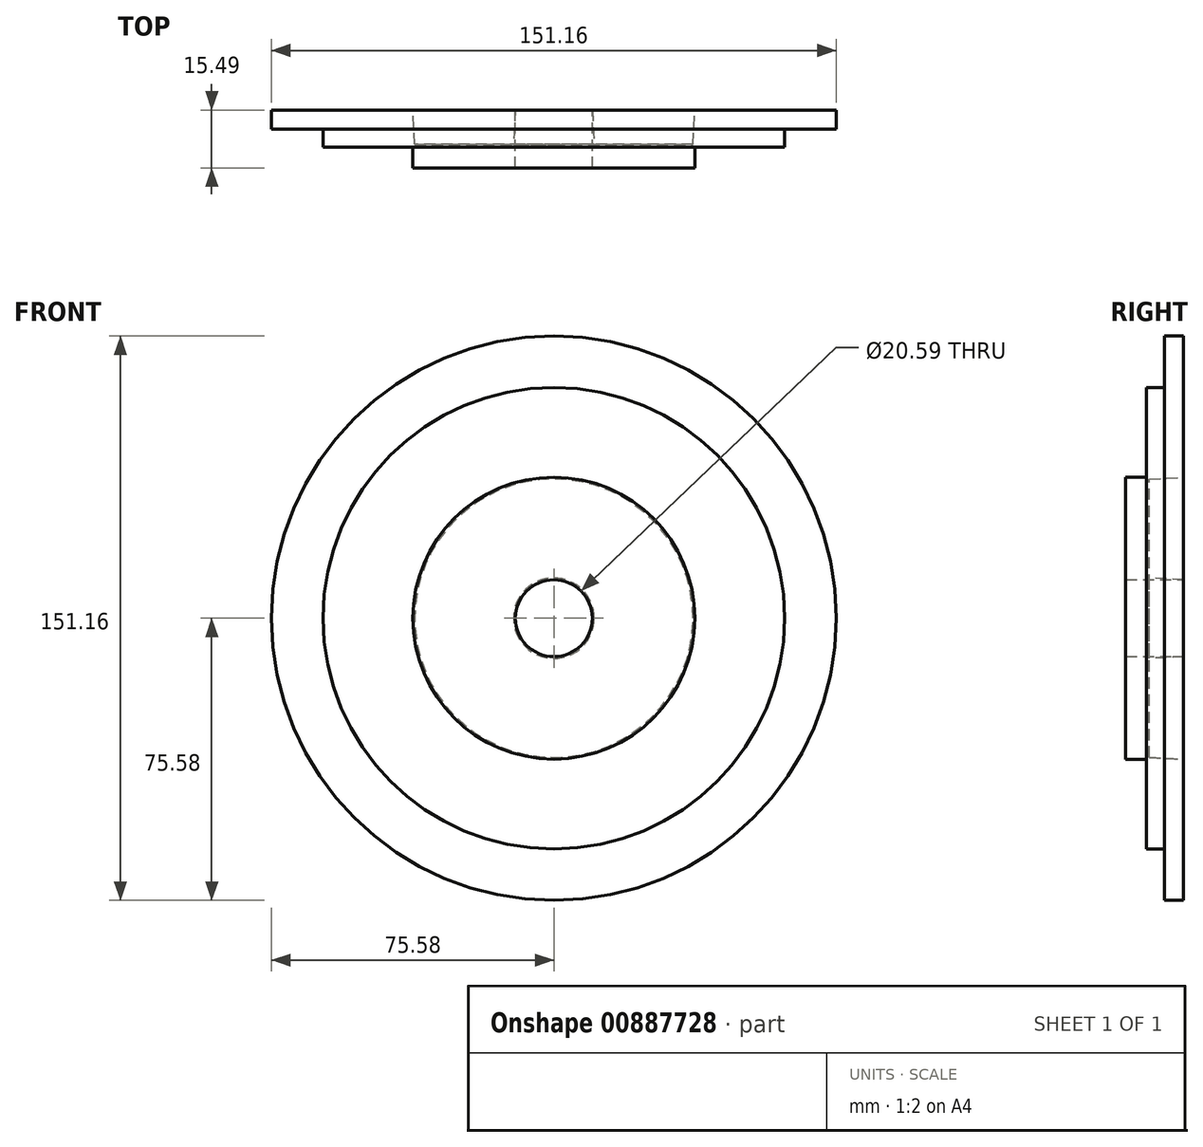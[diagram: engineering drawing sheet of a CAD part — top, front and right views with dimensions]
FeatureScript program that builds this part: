
annotation { "Feature Type Name" : "Feature", "Feature Type Description" : "" }
export const myFeature = defineFeature(function(context is Context, id is Id, definition is map)
    precondition{}
    {
        {
            var Q0;
            Q0=qCreatedBy(makeId("Front.planeOp"),FACE);
            var sketch = newSketch(context, id + "F0", { "sketchPlane" : qUnion([Q0])});
            skCircle(sketch, "E0", {"center": v(0, 0) * mm, "radius": 75.58 * mm});
            skCircle(sketch, "E1", {"center": v(0, 0) * mm, "radius": 37.75 * mm});
            skCircle(sketch, "E2", {"center": v(0, 0) * mm, "radius": 61.8 * mm});
            skCircle(sketch, "E3", {"center": v(0, 0) * mm, "radius": 10.3 * mm});
            skSolve(sketch);
        }
        {
            var Q0;
            Q0 = qSketchRegion(id + "F0", true);
            extrude(context, id + "F1", {"entities" : qUnion([Q0]), "depth" : 5.08 * mm, "offsetDistance" : 25.4 * mm});
        }
        {
            var Q0;
            Q0=makeQuery(id+"F0.imprint","IMPRINT",FACE,{"disambiguationData":[TD([[makeQuery(id+"F0.imprint","IMPRINT",EDGE,{"derivedFrom":sQuery(id+"F0.wireOp",EDGE,"E1")}),-1.0]])]});
            extrude(context, id + "F2", {"entities" : qUnion([Q0]), "operationType" : NewBodyOperationType.ADD, "depth" : 9.9 * mm, "offsetDistance" : 25.4 * mm});
        }
        {
            var Q0;
            Q0=makeQuery(id+"F0.imprint","IMPRINT",FACE,{"disambiguationData":[TD([[makeQuery(id+"F0.imprint","IMPRINT",EDGE,{"derivedFrom":sQuery(id+"F0.wireOp",EDGE,"E1")}),1.0]])]});
            extrude(context, id + "F3", {"entities" : qUnion([Q0]), "operationType" : NewBodyOperationType.ADD, "depth" : 15.5 * mm, "offsetDistance" : 25.4 * mm});
        }
        {
            var Q0;
            Q0=makeQuery(id+"F0.imprint","IMPRINT",FACE,{"disambiguationData":[TD([[makeQuery(id+"F0.imprint","IMPRINT",EDGE,{"derivedFrom":sQuery(id+"F0.wireOp",EDGE,"E1")}),1.0]])]});
            extrude(context, id + "F4", {"entities" : qUnion([Q0]), "operationType" : NewBodyOperationType.ADD, "depth" : 9.9 * mm, "offsetDistance" : 25.4 * mm});
        }
        {
            var Q0;
            Q0=makeQuery(id+"F0.imprint","IMPRINT",FACE,{"disambiguationData":[TD([[makeQuery(id+"F0.imprint","IMPRINT",EDGE,{"derivedFrom":sQuery(id+"F0.wireOp",EDGE,"E1")}),1.0]])]});
            extrude(context, id + "F5", {"entities" : qUnion([Q0]), "operationType" : NewBodyOperationType.REMOVE, "depth" : 9.14 * mm, "offsetDistance" : 25.4 * mm, "hasDraft" : true, "draftAngle" : 3 * degree, "draftPullDirection" : true});
        }
    });
